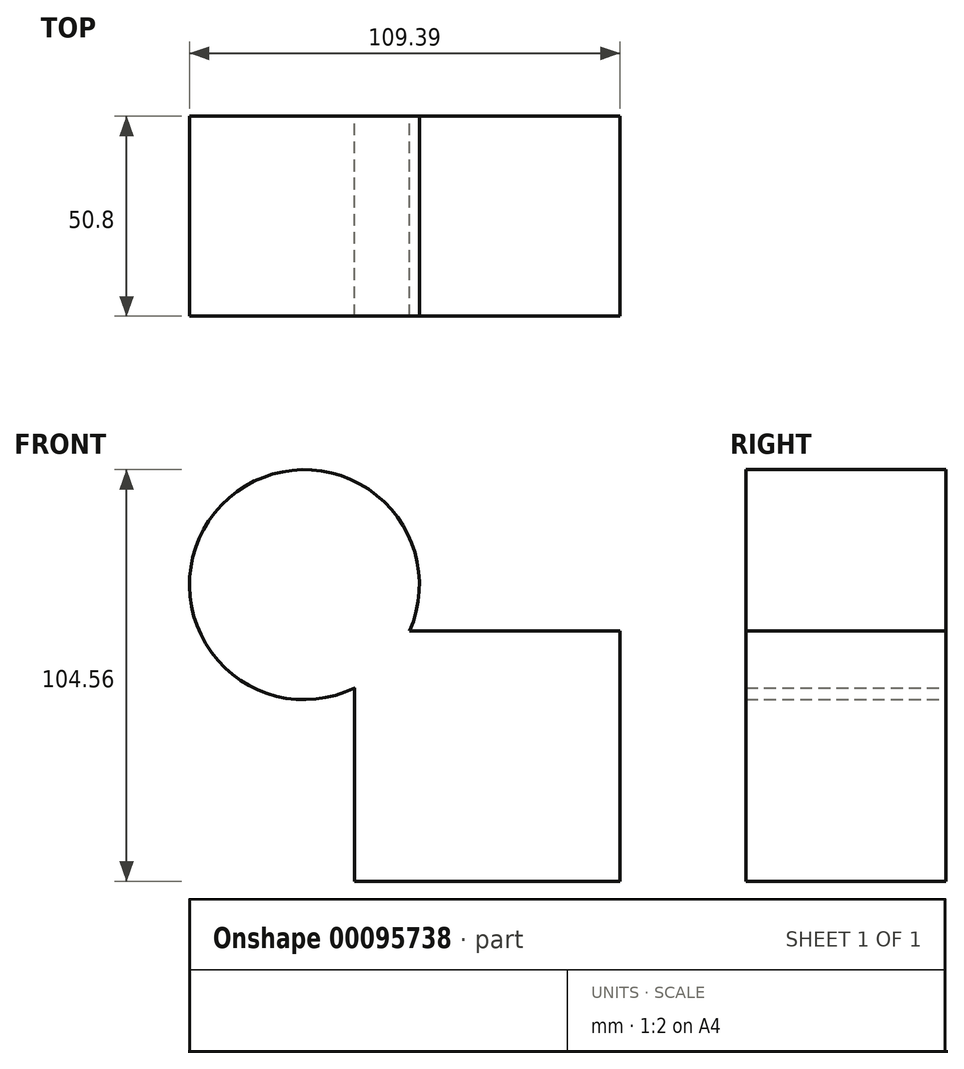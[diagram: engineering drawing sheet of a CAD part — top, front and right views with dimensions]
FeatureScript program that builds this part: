
annotation { "Feature Type Name" : "Feature", "Feature Type Description" : "" }
export const myFeature = defineFeature(function(context is Context, id is Id, definition is map)
    precondition{}
    {
        {
            var Q0;
            Q0=qCreatedBy(makeId("Front.planeOp"),FACE);
            var sketch = newSketch(context, id + "F0", { "sketchPlane" : qUnion([Q0])});
            skLineSegment(sketch, "E0.bottom", {"start": v(-41.58, 45.07) * mm, "end": v(25.81, 45.07) * mm});
            skLineSegment(sketch, "E0.top", {"start": v(-41.58, -18.53) * mm, "end": v(25.81, -18.53) * mm});
            skLineSegment(sketch, "E0.left", {"start": v(-41.58, 45.07) * mm, "end": v(-41.58, -18.53) * mm});
            skLineSegment(sketch, "E0.right", {"start": v(25.81, 45.07) * mm, "end": v(25.81, -18.53) * mm});
            skCircle(sketch, "E1", {"center": v(-54.37, 56.82) * mm, "radius": 29.2 * mm});
            skSolve(sketch);
        }
        {
            var Q0;
            Q0 = qSketchRegion(id + "F0", true);
            extrude(context, id + "F1", {"entities" : qUnion([Q0]), "depth" : 50.8 * mm});
        }
    });
